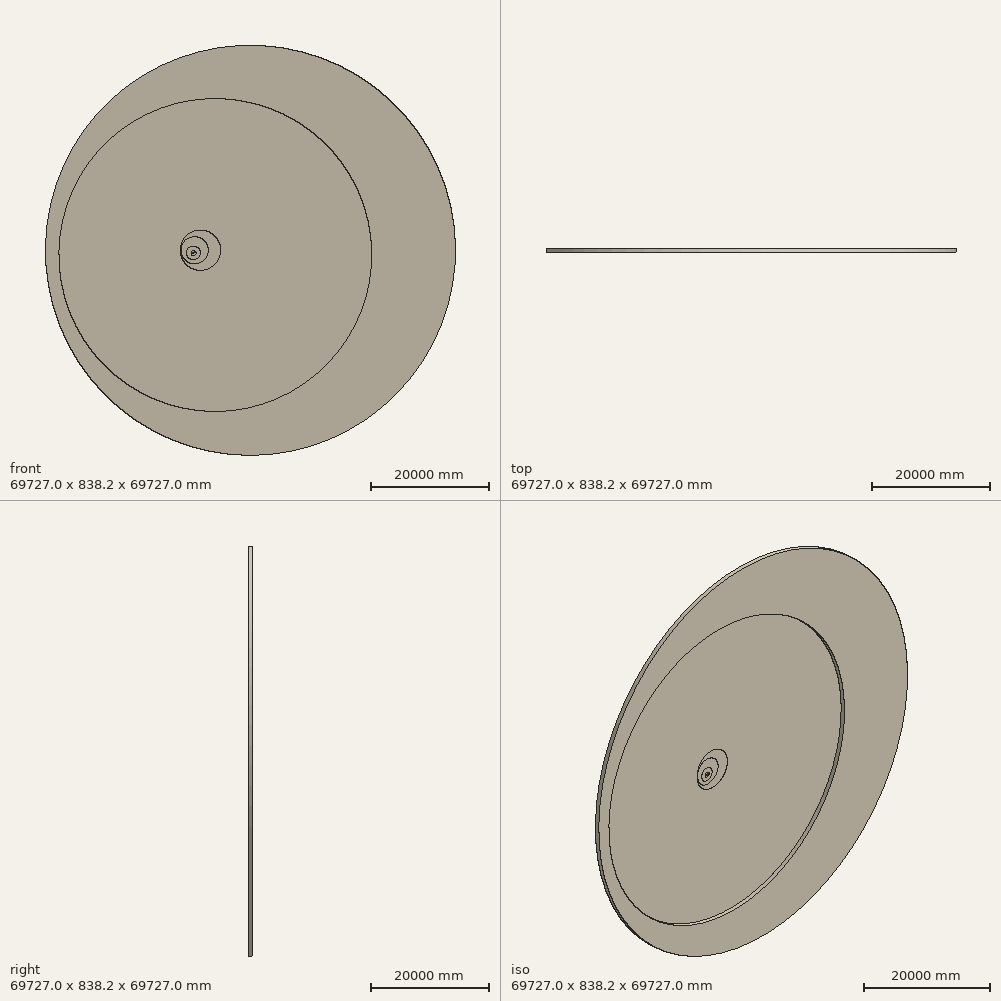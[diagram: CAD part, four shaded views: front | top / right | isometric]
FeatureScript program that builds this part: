
annotation { "Feature Type Name" : "Feature", "Feature Type Description" : "" }
export const myFeature = defineFeature(function(context is Context, id is Id, definition is map)
    precondition{}
    {
        {
            var Q0;
            Q0=qCreatedBy(makeId("Front.planeOp"),FACE);
            var sketch = newSketch(context, id + "F0", { "sketchPlane" : qUnion([Q0])});
            skCircle(sketch, "E0", {"center": v(-7.1, -8.98) * mm, "radius": 72 * mm});
            skSolve(sketch);
        }
        {
            var Q0;
            Q0=makeQuery(id+"F0.imprint","IMPRINT",FACE,{"disambiguationData":[TD([[makeQuery(id+"F0.imprint","IMPRINT",EDGE,{"derivedFrom":sQuery(id+"F0.wireOp",EDGE,"E0")}),1.0]])]});
            extrude(context, id + "F1", {"entities" : qUnion([Q0]), "depth" : 101.6 * mm});
        }
        {
            var Q0;
            Q0=makeQuery(id+"F1.opExtrude","CAP_FACE",FACE,{"disambiguationData":[OSD([sQuery(id+"F0.wireOp",EDGE,"E0")])],"isStart":false});
            var sketch = newSketch(context, id + "F2", { "sketchPlane" : qUnion([Q0])});
            skCircle(sketch, "E1", {"center": v(-15.28, -1.21) * mm, "radius": 136.12 * mm});
            skSolve(sketch);
        }
        {
            var Q0;
            Q0=makeQuery(id+"F2.imprint","IMPRINT",FACE,{"disambiguationData":[TD([[makeQuery(id+"F2.imprint","IMPRINT",EDGE,{"derivedFrom":sQuery(id+"F2.wireOp",EDGE,"E1")}),1.0]])]});
            extrude(context, id + "F3", {"entities" : qUnion([Q0]), "depth" : 25.4 * mm});
        }
        {
            var Q0;
            Q0=makeQuery(id+"F1.opExtrude","CAP_FACE",FACE,{"disambiguationData":[OSD([sQuery(id+"F0.wireOp",EDGE,"E0")])],"isStart":false});
            var sketch = newSketch(context, id + "F4", { "sketchPlane" : qUnion([Q0])});
            skCircle(sketch, "E2", {"center": v(-5.64, -5.54) * mm, "radius": 181.87 * mm});
            skCircle(sketch, "E3", {"center": v(33.43, 65.57) * mm, "radius": 159.6 * mm});
            skSolve(sketch);
        }
        {
            var Q0;
            Q0=makeQuery(id+"F4.imprint","IMPRINT",FACE,{"disambiguationData":[TD([[makeQuery(id+"F4.imprint","IMPRINT",EDGE,{"derivedFrom":makeQuery(id+"F1.opExtrude","CAP_EDGE",EDGE,{"disambiguationData":[OSD([sQuery(id+"F0.wireOp",EDGE,"E0")])],"isStart":false})}),-1.0]])]});
            extrude(context, id + "F5", {"entities" : qUnion([Q0]), "operationType" : NewBodyOperationType.ADD, "depth" : 25.4 * mm});
        }
        {
            var Q0;
            Q0=makeQuery(id+"F1.opExtrude","CAP_FACE",FACE,{"disambiguationData":[OSD([sQuery(id+"F0.wireOp",EDGE,"E0")])],"isStart":true});
            var sketch = newSketch(context, id + "F6", { "sketchPlane" : qUnion([Q0])});
            skCircle(sketch, "E4", {"center": v(-45.52, -48.9) * mm, "radius": 431.4 * mm});
            skSolve(sketch);
        }
        {
            var Q0;
            Q0=makeQuery(id+"F6.imprint","IMPRINT",FACE,{"disambiguationData":[TD([[makeQuery(id+"F6.imprint","IMPRINT",EDGE,{"derivedFrom":sQuery(id+"F6.wireOp",EDGE,"E4")}),1.0]])]});
            extrude(context, id + "F7", {"entities" : qUnion([Q0]), "depth" : 25.4 * mm});
        }
        {
            var Q0;
            Q0=makeQuery(id+"F7.opExtrude","CAP_FACE",FACE,{"disambiguationData":[OSD([sQuery(id+"F0.wireOp",EDGE,"E0"),sQuery(id+"F6.wireOp",EDGE,"E4")])],"isStart":false});
            var sketch = newSketch(context, id + "F8", { "sketchPlane" : qUnion([Q0])});
            skSolve(sketch);
        }
        {
            var Q0;
            Q0=makeQuery(id+"F8.imprint","IMPRINT",FACE,{"disambiguationData":[TD([[makeQuery(id+"F8.imprint","IMPRINT",EDGE,{"derivedFrom":makeQuery(id+"F7.opExtrude","CAP_EDGE",EDGE,{"disambiguationData":[OSD([sQuery(id+"F6.wireOp",EDGE,"E4")])],"isStart":false})}),1.0]])]});
            var sketch = newSketch(context, id + "F9", { "sketchPlane" : qUnion([Q0])});
            skCircle(sketch, "E5", {"center": v(4.56, 7) * mm, "radius": 1168.6 * mm});
            skSolve(sketch);
        }
        {
            var Q0;
            Q0=makeQuery(id+"F9.imprint","IMPRINT",FACE,{"disambiguationData":[TD([[makeQuery(id+"F9.imprint","IMPRINT",EDGE,{"derivedFrom":sQuery(id+"F9.wireOp",EDGE,"E5")}),1.0]])]});
            extrude(context, id + "F10", {"entities" : qUnion([Q0]), "depth" : 25.4 * mm});
        }
        {
            var Q0;
            Q0=makeQuery(id+"F10.opExtrude","CAP_FACE",FACE,{"disambiguationData":[OSD([sQuery(id+"F6.wireOp",EDGE,"E4"),sQuery(id+"F9.wireOp",EDGE,"E5")])],"isStart":false});
            var sketch = newSketch(context, id + "F11", { "sketchPlane" : qUnion([Q0])});
            skCircle(sketch, "E6", {"center": v(-212.74, 451.75) * mm, "radius": 2317.19 * mm});
            skSolve(sketch);
        }
        {
            var Q0;
            Q0=makeQuery(id+"F11.imprint","IMPRINT",FACE,{"disambiguationData":[TD([[makeQuery(id+"F11.imprint","IMPRINT",EDGE,{"derivedFrom":sQuery(id+"F11.wireOp",EDGE,"E6")}),1.0]])]});
            extrude(context, id + "F12", {"entities" : qUnion([Q0]), "depth" : 25.4 * mm});
        }
        {
            var Q0;
            Q0=makeQuery(id+"F12.opExtrude","CAP_FACE",FACE,{"disambiguationData":[OSD([sQuery(id+"F9.wireOp",EDGE,"E5"),sQuery(id+"F11.wireOp",EDGE,"E6")])],"isStart":false});
            var sketch = newSketch(context, id + "F13", { "sketchPlane" : qUnion([Q0])});
            skCircle(sketch, "E7", {"center": v(-1206.54, 460.44) * mm, "radius": 3434.58 * mm});
            skSolve(sketch);
        }
        {
            var Q0;
            Q0=makeQuery(id+"F13.imprint","IMPRINT",FACE,{"disambiguationData":[TD([[makeQuery(id+"F13.imprint","IMPRINT",EDGE,{"derivedFrom":sQuery(id+"F13.wireOp",EDGE,"E7")}),1.0]])]});
            extrude(context, id + "F14", {"entities" : qUnion([Q0]), "depth" : 25.4 * mm});
        }
        {
            var Q0;
            Q0=makeQuery(id+"F14.opExtrude","CAP_FACE",FACE,{"disambiguationData":[OSD([sQuery(id+"F11.wireOp",EDGE,"E6"),sQuery(id+"F13.wireOp",EDGE,"E7")])],"isStart":false});
            var sketch = newSketch(context, id + "F15", { "sketchPlane" : qUnion([Q0])});
            skCircle(sketch, "E8", {"center": v(-2529.92, 457.65) * mm, "radius": 43904.12 * mm});
            skSolve(sketch);
        }
        {
            var Q0;
            Q0=makeQuery(id+"F15.imprint","IMPRINT",FACE,{"disambiguationData":[TD([[makeQuery(id+"F15.imprint","IMPRINT",EDGE,{"derivedFrom":makeQuery(id+"F14.opExtrude","CAP_EDGE",EDGE,{"disambiguationData":[OSD([sQuery(id+"F11.wireOp",EDGE,"E6")])],"isStart":false})}),1.0]])]});
            var Q1;
            Q1=makeQuery(id+"F15.imprint","IMPRINT",FACE,{"disambiguationData":[TD([[makeQuery(id+"F15.imprint","IMPRINT",EDGE,{"derivedFrom":makeQuery(id+"F14.opExtrude","CAP_EDGE",EDGE,{"disambiguationData":[OSD([sQuery(id+"F13.wireOp",EDGE,"E7")])],"isStart":false})}),1.0]])]});
            extrude(context, id + "F16", {"entities" : qUnion([Q0, Q1]), "operationType" : NewBodyOperationType.ADD, "depth" : 25.4 * mm});
        }
        {
            var Q0;
            Q0=makeQuery(id+"F14.opExtrude","CAP_FACE",FACE,{"disambiguationData":[OSD([sQuery(id+"F11.wireOp",EDGE,"E6"),sQuery(id+"F13.wireOp",EDGE,"E7")])],"isStart":true});
            var sketch = newSketch(context, id + "F17", { "sketchPlane" : qUnion([Q0])});
            skCircle(sketch, "E9", {"center": v(3713.37, -348.75) * mm, "radius": 26604.09 * mm});
            skSolve(sketch);
        }
        {
            var Q0;
            Q0=makeQuery(id+"F17.imprint","IMPRINT",FACE,{"disambiguationData":[TD([[makeQuery(id+"F17.imprint","IMPRINT",EDGE,{"derivedFrom":sQuery(id+"F17.wireOp",EDGE,"E9")}),1.0]])]});
            extrude(context, id + "F18", {"entities" : qUnion([Q0]), "depth" : 25.4 * mm});
        }
        {
            var Q0;
            Q0=makeQuery(id+"F18.opExtrude","CAP_FACE",FACE,{"disambiguationData":[OSD([sQuery(id+"F13.wireOp",EDGE,"E7"),sQuery(id+"F17.wireOp",EDGE,"E9")])],"isStart":false});
            var sketch = newSketch(context, id + "F19", { "sketchPlane" : qUnion([Q0])});
            skCircle(sketch, "E10", {"center": v(9687.33, 450.54) * mm, "radius": 34863.5 * mm});
            skSolve(sketch);
        }
        {
            var Q0;
            Q0=makeQuery(id+"F19.imprint","IMPRINT",FACE,{"disambiguationData":[TD([[makeQuery(id+"F19.imprint","IMPRINT",EDGE,{"derivedFrom":sQuery(id+"F19.wireOp",EDGE,"E10")}),1.0]])]});
            extrude(context, id + "F20", {"entities" : qUnion([Q0]), "depth" : 762 * mm});
        }
    });
